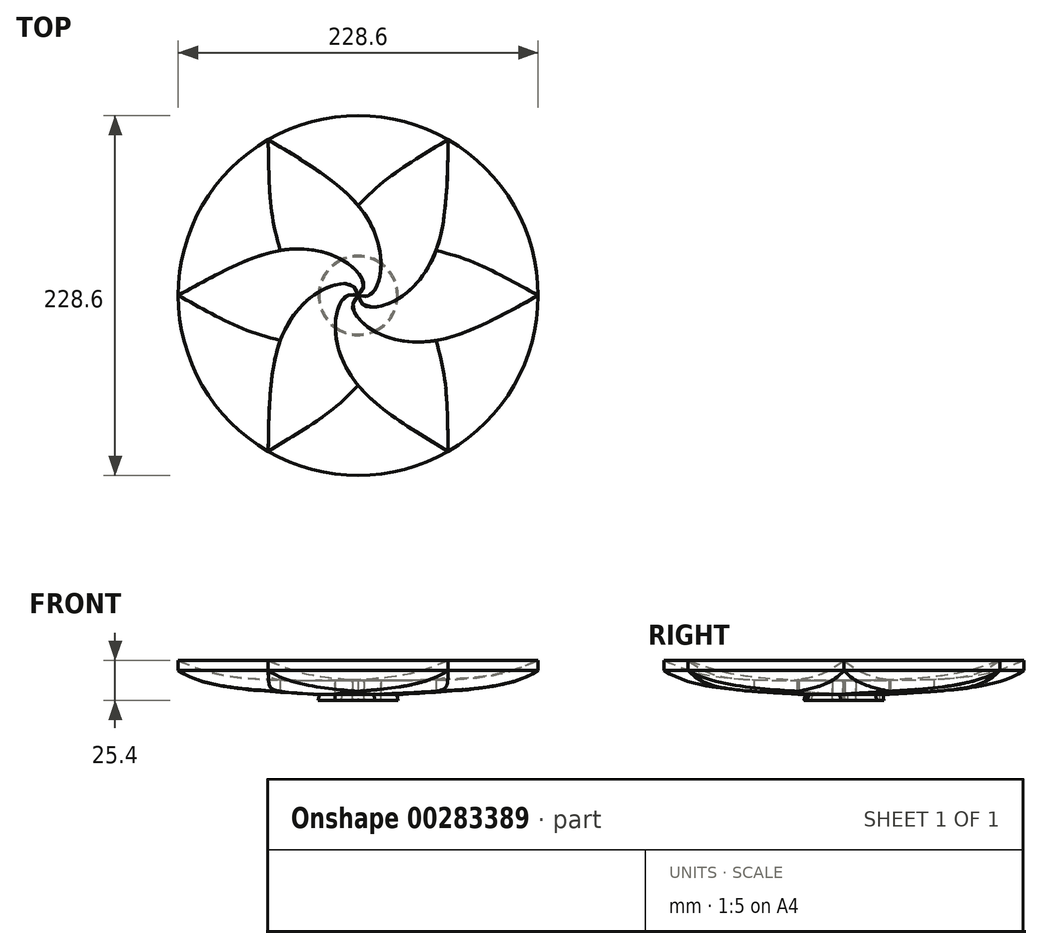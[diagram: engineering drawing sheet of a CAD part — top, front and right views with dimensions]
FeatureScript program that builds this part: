
annotation { "Feature Type Name" : "Feature", "Feature Type Description" : "" }
export const myFeature = defineFeature(function(context is Context, id is Id, definition is map)
    precondition{}
    {
        {
            var Q0;
            Q0=qCreatedBy(makeId("Top.planeOp"),FACE);
            var sketch = newSketch(context, id + "F0", { "sketchPlane" : qUnion([Q0])});
            skLineSegment(sketch, "E0", {"start": v(0, 0) * mm, "end": v(114.3, 0) * mm, "construction": true});
            skCircle(sketch, "E1.cCircle", {"center": v(0, 0) * mm, "radius": 114.3 * mm, "construction": true});
            skLineSegment(sketch, "E1.0", {"start": v(114.3, 66) * mm, "end": v(114.3, -66) * mm, "construction": true});
            skLineSegment(sketch, "E1.1", {"start": v(114.3, -66) * mm, "end": v(0, -131.98) * mm, "construction": true});
            skLineSegment(sketch, "E1.2", {"start": v(0, -131.98) * mm, "end": v(-114.3, -66) * mm, "construction": true});
            skLineSegment(sketch, "E1.3", {"start": v(-114.3, -66) * mm, "end": v(-114.3, 66) * mm, "construction": true});
            skLineSegment(sketch, "E1.4", {"start": v(-114.3, 66) * mm, "end": v(0, 131.98) * mm, "construction": true});
            skLineSegment(sketch, "E1.5", {"start": v(0, 131.98) * mm, "end": v(114.3, 66) * mm, "construction": true});
            skPoint(sketch, "E1.0.midPoint", {"position": v(114.3, 0) * mm});
            skLineSegment(sketch, "E2", {"start": v(0, 0) * mm, "end": v(114.3, 66) * mm, "construction": true});
            skLineSegment(sketch, "E3", {"start": v(0, 0) * mm, "end": v(0, 131.98) * mm, "construction": true});
            skLineSegment(sketch, "E4", {"start": v(0, 0) * mm, "end": v(57.15, 98.99) * mm, "construction": true});
            skLineSegment(sketch, "E5", {"start": v(0, 0) * mm, "end": v(0, 57.15) * mm, "construction": true});
            skLineSegment(sketch, "E6", {"start": v(0, 0) * mm, "end": v(14.29, 24.75) * mm, "construction": true});
            skLineSegment(sketch, "E7", {"start": v(0, 0) * mm, "end": v(12.37, 7.14) * mm, "construction": true});
            skLineSegment(sketch, "E8", {"start": v(0, 0) * mm, "end": v(7.14, 0) * mm, "construction": true});
            skFitSpline(sketch, "E9", {"points": [v(-57.15, 98.99) * mm, v(0, 57.15) * mm, v(14.29, 24.75) * mm, v(12.37, 7.14) * mm, v(7.14, 0) * mm, v(0, 0) * mm], "startDerivative": vector(191.8, -114.67) * mm, "endDerivative": vector(-69.14, 12.61) * mm});
            skLineSegment(sketch, "E10", {"start": v(0, 0) * mm, "end": v(114.3, -66) * mm, "construction": true});
            skLineSegment(sketch, "E11", {"start": v(0, 0) * mm, "end": v(57.15, -98.99) * mm, "construction": true});
            skLineSegment(sketch, "E12", {"start": v(0, 0) * mm, "end": v(49.5, 28.58) * mm, "construction": true});
            skLineSegment(sketch, "E13", {"start": v(0, 0) * mm, "end": v(28.58, 0) * mm, "construction": true});
            skLineSegment(sketch, "E14", {"start": v(0, 0) * mm, "end": v(12.37, -7.14) * mm, "construction": true});
            skLineSegment(sketch, "E15", {"start": v(0, 0) * mm, "end": v(3.57, -6.19) * mm, "construction": true});
            skFitSpline(sketch, "E16", {"points": [v(57.15, 98.99) * mm, v(49.5, 28.57) * mm, v(28.58, 0) * mm, v(12.37, -7.14) * mm, v(3.57, -6.19) * mm, v(0, 0) * mm], "startDerivative": vector(-3.41, -223.44) * mm, "endDerivative": vector(-23.64, 66.18) * mm});
            skLineSegment(sketch, "E17", {"start": v(28.57, 115.48) * mm, "end": v(0, 0) * mm, "construction": true});
            skLineSegment(sketch, "E18", {"start": v(0, 0) * mm, "end": v(18.3, 73.97) * mm, "construction": true});
            skFitSpline(sketch, "E19", {"points": [v(57.15, 98.99) * mm, v(18.3, 73.97) * mm, v(0, 57.15) * mm], "startDerivative": vector(-74.29, -44.4) * mm, "endDerivative": vector(-38.16, -38.99) * mm});
            skSolve(sketch);
        }
        {
            var Q0;
            Q0=makeQuery(id+"F0.imprint","IMPRINT",FACE,{"disambiguationData":[TD([[makeQuery(id+"F0.imprint","IMPRINT",EDGE,{"derivedFrom":sQuery(id+"F0.wireOp",EDGE,"E9")}),1.0]])]});
            extrude(context, id + "F1", {"entities" : qUnion([Q0]), "depth" : 25.4 * mm});
        }
        {
            var Q0;
            Q0=makeQuery(id+"F1.opExtrude","SWEPT_BODY",BODY,{"disambiguationData":[OSD([sQuery(id+"F0.wireOp",EDGE,"E9"),sQuery(id+"F0.wireOp",EDGE,"TZXXsanI-fCTB-etiP-ZLQ6-q0ArW132sDCA"),sQuery(id+"F0.wireOp",EDGE,"e2zwRiE5-dgJw-LFtH-64ea-Jk8bidKStY3W"),sQuery(id+"F0.wireOp",EDGE,"E16")])]});
            var Q1;
            Q1=makeQuery(id+"F1.opExtrude","SWEPT_EDGE",EDGE,{"disambiguationData":[OSD([sQuery(id+"F0.wireOp",EDGE,"E9"),sQuery(id+"F0.wireOp",EDGE,"E16")])]});
            transform(context, id + "F2", {"entities" : qUnion([Q0]), "transformType" : TransformType.ROTATION, "transformAxis" : qUnion([Q1]), "angle" : 60 * degree, "makeCopy" : true});
        }
        {
            var Q0;
            Q0=makeQuery(id+"F2.opPattern","COPY",BODY,{"derivedFrom":makeQuery(id+"F1.opExtrude","SWEPT_BODY",BODY,{"disambiguationData":[OSD([sQuery(id+"F0.wireOp",EDGE,"E9"),sQuery(id+"F0.wireOp",EDGE,"TZXXsanI-fCTB-etiP-ZLQ6-q0ArW132sDCA"),sQuery(id+"F0.wireOp",EDGE,"e2zwRiE5-dgJw-LFtH-64ea-Jk8bidKStY3W"),sQuery(id+"F0.wireOp",EDGE,"E16")])]}),"instanceName":"1"});
            var Q1;
            Q1=makeQuery(id+"F1.opExtrude","SWEPT_EDGE",EDGE,{"disambiguationData":[OSD([sQuery(id+"F0.wireOp",EDGE,"E9"),sQuery(id+"F0.wireOp",EDGE,"E16")])]});
            transform(context, id + "F3", {"entities" : qUnion([Q0]), "transformType" : TransformType.ROTATION, "transformAxis" : qUnion([Q1]), "angle" : 60 * degree, "makeCopy" : true});
        }
        {
            var Q0;
            Q0=makeQuery(id+"F3.opPattern","COPY",BODY,{"derivedFrom":makeQuery(id+"F2.opPattern","COPY",BODY,{"derivedFrom":makeQuery(id+"F1.opExtrude","SWEPT_BODY",BODY,{"disambiguationData":[OSD([sQuery(id+"F0.wireOp",EDGE,"E9"),sQuery(id+"F0.wireOp",EDGE,"TZXXsanI-fCTB-etiP-ZLQ6-q0ArW132sDCA"),sQuery(id+"F0.wireOp",EDGE,"e2zwRiE5-dgJw-LFtH-64ea-Jk8bidKStY3W"),sQuery(id+"F0.wireOp",EDGE,"E16")])]}),"instanceName":"1"}),"instanceName":"1"});
            var Q1;
            Q1=makeQuery(id+"F2.opPattern","COPY",BODY,{"derivedFrom":makeQuery(id+"F1.opExtrude","SWEPT_BODY",BODY,{"disambiguationData":[OSD([sQuery(id+"F0.wireOp",EDGE,"E9"),sQuery(id+"F0.wireOp",EDGE,"TZXXsanI-fCTB-etiP-ZLQ6-q0ArW132sDCA"),sQuery(id+"F0.wireOp",EDGE,"e2zwRiE5-dgJw-LFtH-64ea-Jk8bidKStY3W"),sQuery(id+"F0.wireOp",EDGE,"E16")])]}),"instanceName":"1"});
            var Q2;
            Q2=makeQuery(id+"F1.opExtrude","SWEPT_BODY",BODY,{"disambiguationData":[OSD([sQuery(id+"F0.wireOp",EDGE,"E9"),sQuery(id+"F0.wireOp",EDGE,"TZXXsanI-fCTB-etiP-ZLQ6-q0ArW132sDCA"),sQuery(id+"F0.wireOp",EDGE,"e2zwRiE5-dgJw-LFtH-64ea-Jk8bidKStY3W"),sQuery(id+"F0.wireOp",EDGE,"E16")])]});
            var Q3;
            Q3=makeQuery(id+"F1.opExtrude","SWEPT_EDGE",EDGE,{"disambiguationData":[OSD([sQuery(id+"F0.wireOp",EDGE,"E9"),sQuery(id+"F0.wireOp",EDGE,"E16")])]});
            transform(context, id + "F4", {"entities" : qUnion([Q0, Q1, Q2]), "transformType" : TransformType.ROTATION, "transformAxis" : qUnion([Q3]), "angle" : 180 * degree, "makeCopy" : true});
        }
        {
            var Q0;
            Q0=makeQuery(id+"F4.opPattern","COPY",FACE,{"derivedFrom":makeQuery(id+"F3.opPattern","COPY",FACE,{"derivedFrom":makeQuery(id+"F2.opPattern","COPY",FACE,{"derivedFrom":makeQuery(id+"F1.opExtrude","CAP_FACE",FACE,{"disambiguationData":[OSD([sQuery(id+"F0.wireOp",EDGE,"E9"),sQuery(id+"F0.wireOp",EDGE,"E16"),sQuery(id+"F0.wireOp",EDGE,"E19")])],"isStart":false}),"instanceName":"1"}),"instanceName":"1"}),"instanceName":"1"});
            var sketch = newSketch(context, id + "F5", { "sketchPlane" : qUnion([Q0])});
            skCircle(sketch, "E20", {"center": v(0, 0) * mm, "radius": 114.3 * mm});
            skSolve(sketch);
        }
        {
            var Q0;
            Q0=makeQuery(id+"F5.imprint","IMPRINT",FACE,{"disambiguationData":[TD([[makeQuery(id+"F5.imprint","IMPRINT",EDGE,{"derivedFrom":sQuery(id+"F5.wireOp",EDGE,"E20")}),1.0]])]});
            var Q1;
            Q1=makeQuery(id+"F5.imprint","IMPRINT",FACE,{"disambiguationData":[TD([[makeQuery(id+"F5.imprint","IMPRINT",EDGE,{"derivedFrom":makeQuery(id+"F4.opPattern","COPY",EDGE,{"derivedFrom":makeQuery(id+"F3.opPattern","COPY",EDGE,{"derivedFrom":makeQuery(id+"F2.opPattern","COPY",EDGE,{"derivedFrom":makeQuery(id+"F1.opExtrude","CAP_EDGE",EDGE,{"disambiguationData":[OSD([sQuery(id+"F0.wireOp",EDGE,"E9")])],"isStart":false}),"instanceName":"1"}),"instanceName":"1"}),"instanceName":"1"})}),1.0]])]});
            extrude(context, id + "F6", {"entities" : qUnion([Q0, Q1]), "oppositeDirection" : true, "depth" : 25.4 * mm});
        }
        {
            var Q0;
            Q0=makeQuery(id+"F2.opPattern","COPY",BODY,{"derivedFrom":makeQuery(id+"F1.opExtrude","SWEPT_BODY",BODY,{"disambiguationData":[OSD([sQuery(id+"F0.wireOp",EDGE,"E9"),sQuery(id+"F0.wireOp",EDGE,"E16"),sQuery(id+"F0.wireOp",EDGE,"E19")])]}),"instanceName":"1"});
            var Q1;
            Q1=makeQuery(id+"F4.opPattern","COPY",BODY,{"derivedFrom":makeQuery(id+"F2.opPattern","COPY",BODY,{"derivedFrom":makeQuery(id+"F1.opExtrude","SWEPT_BODY",BODY,{"disambiguationData":[OSD([sQuery(id+"F0.wireOp",EDGE,"E9"),sQuery(id+"F0.wireOp",EDGE,"E16"),sQuery(id+"F0.wireOp",EDGE,"E19")])]}),"instanceName":"1"}),"instanceName":"1"});
            var Q2;
            Q2=makeQuery(id+"F3.opPattern","COPY",BODY,{"derivedFrom":makeQuery(id+"F2.opPattern","COPY",BODY,{"derivedFrom":makeQuery(id+"F1.opExtrude","SWEPT_BODY",BODY,{"disambiguationData":[OSD([sQuery(id+"F0.wireOp",EDGE,"E9"),sQuery(id+"F0.wireOp",EDGE,"E16"),sQuery(id+"F0.wireOp",EDGE,"E19")])]}),"instanceName":"1"}),"instanceName":"1"});
            var Q3;
            Q3=makeQuery(id+"F4.opPattern","COPY",BODY,{"derivedFrom":makeQuery(id+"F1.opExtrude","SWEPT_BODY",BODY,{"disambiguationData":[OSD([sQuery(id+"F0.wireOp",EDGE,"E9"),sQuery(id+"F0.wireOp",EDGE,"E16"),sQuery(id+"F0.wireOp",EDGE,"E19")])]}),"instanceName":"1"});
            var Q4;
            Q4=makeQuery(id+"F4.opPattern","COPY",BODY,{"derivedFrom":makeQuery(id+"F3.opPattern","COPY",BODY,{"derivedFrom":makeQuery(id+"F2.opPattern","COPY",BODY,{"derivedFrom":makeQuery(id+"F1.opExtrude","SWEPT_BODY",BODY,{"disambiguationData":[OSD([sQuery(id+"F0.wireOp",EDGE,"E9"),sQuery(id+"F0.wireOp",EDGE,"E16"),sQuery(id+"F0.wireOp",EDGE,"E19")])]}),"instanceName":"1"}),"instanceName":"1"}),"instanceName":"1"});
            var Q5;
            Q5=makeQuery(id+"F1.opExtrude","SWEPT_BODY",BODY,{"disambiguationData":[OSD([sQuery(id+"F0.wireOp",EDGE,"E9"),sQuery(id+"F0.wireOp",EDGE,"E16"),sQuery(id+"F0.wireOp",EDGE,"E19")])]});
            var Q6;
            Q6=makeQuery(id+"F6.opExtrude","SWEPT_BODY",BODY,{"disambiguationData":[OSD([sQuery(id+"F5.wireOp",EDGE,"E20")])]});
            booleanBodies(context, id + "F7", {"operationType" : BooleanOperationType.SUBTRACTION, "tools" : qUnion([Q0, Q1, Q2, Q3, Q4, Q5]), "targets" : qUnion([Q6]), "keepTools" : true});
        }
        {
            var Q0;
            Q0=qCreatedBy(makeId("Front.planeOp"),FACE);
            var sketch = newSketch(context, id + "F8", { "sketchPlane" : qUnion([Q0])});
            skLineSegment(sketch, "E21", {"start": v(0, 0) * mm, "end": v(0, 12.7) * mm});
            skLineSegment(sketch, "E22", {"start": v(0, 12.7) * mm, "end": v(-114.3, 12.7) * mm, "construction": true});
            skLineSegment(sketch, "E23", {"start": v(-114.3, 12.7) * mm, "end": v(-114.3, 25.4) * mm, "construction": true});
            skFitSpline(sketch, "E24", {"points": [v(-114.3, 25.4) * mm, v(-77, 14.6) * mm, v(0, 12.7) * mm], "startDerivative": vector(90.35, -40.4) * mm, "endDerivative": vector(131.25, 0) * mm});
            skLineSegment(sketch, "E25", {"start": v(0, 0) * mm, "end": v(-25.4, 0) * mm});
            skLineSegment(sketch, "E26", {"start": v(-25.4, 0) * mm, "end": v(-24.56, 3.65) * mm});
            skLineSegment(sketch, "E27", {"start": v(-114.3, 25.4) * mm, "end": v(-114.3, 19.05) * mm});
            skFitSpline(sketch, "E28", {"points": [v(-114.3, 19.05) * mm, v(-80.58, 8.1) * mm, v(-24.56, 3.65) * mm], "startDerivative": vector(65.57, -43.03) * mm, "endDerivative": vector(113.17, -7.4) * mm});
            skSolve(sketch);
        }
        {
            var Q0;
            Q0 = qSketchRegion(id + "F8", true);
            var Q1;
            Q1=sQuery(id+"F8.wireOp",EDGE,"E21");
            revolve(context, id + "F9", {"entities" : qUnion([Q0]), "axis" : qUnion([Q1]), "revolveType" : RevolveType.FULL});
        }
        {
            var Q0;
            Q0=qCreatedBy(makeId("Top.planeOp"),FACE);
            var sketch = newSketch(context, id + "F10", { "sketchPlane" : qUnion([Q0])});
            skCircle(sketch, "E29", {"center": v(0, 0) * mm, "radius": 127 * mm});
            skSolve(sketch);
        }
        {
            var Q0;
            Q0=makeQuery(id+"F10.imprint","IMPRINT",FACE,{"disambiguationData":[TD([[makeQuery(id+"F10.imprint","IMPRINT",EDGE,{"derivedFrom":sQuery(id+"F10.wireOp",EDGE,"E29")}),1.0]])]});
            extrude(context, id + "F11", {"entities" : qUnion([Q0]), "depth" : 25.4 * mm});
        }
        {
            var Q0;
            Q0=makeQuery(id+"F9.opRevolve","SWEPT_BODY",BODY,{"disambiguationData":[OSD([sQuery(id+"F8.wireOp",EDGE,"E21"),sQuery(id+"F8.wireOp",EDGE,"E24"),sQuery(id+"F8.wireOp",EDGE,"E25"),sQuery(id+"F8.wireOp",EDGE,"E26"),sQuery(id+"F8.wireOp",EDGE,"E27"),sQuery(id+"F8.wireOp",EDGE,"E28")])]});
            var Q1;
            Q1=makeQuery(id+"F11.opExtrude","SWEPT_BODY",BODY,{"disambiguationData":[OSD([sQuery(id+"F10.wireOp",EDGE,"E29")])]});
            booleanBodies(context, id + "F12", {"operationType" : BooleanOperationType.SUBTRACTION, "tools" : qUnion([Q0]), "targets" : qUnion([Q1])});
        }
        {
            var Q0;
            Q0=makeQuery(id+"F12.opBoolean","SPLIT",BODY,{"disambiguationData":[OD(1.0)],"derivedFrom":makeQuery(id+"F11.opExtrude","SWEPT_BODY",BODY,{"disambiguationData":[OSD([sQuery(id+"F10.wireOp",EDGE,"E29")])]})});
            var Q1;
            Q1=makeQuery(id+"F12.opBoolean","SPLIT",BODY,{"disambiguationData":[OD(0.0)],"derivedFrom":makeQuery(id+"F11.opExtrude","SWEPT_BODY",BODY,{"disambiguationData":[OSD([sQuery(id+"F10.wireOp",EDGE,"E29")])]})});
            var Q2;
            Q2=makeQuery(id+"F7.opBoolean","SPLIT",BODY,{"disambiguationData":[OD(5.0)],"derivedFrom":makeQuery(id+"F6.opExtrude","SWEPT_BODY",BODY,{"disambiguationData":[OSD([sQuery(id+"F5.wireOp",EDGE,"E20")])]})});
            var Q3;
            Q3=makeQuery(id+"F1.opExtrude","SWEPT_BODY",BODY,{"disambiguationData":[OSD([sQuery(id+"F0.wireOp",EDGE,"E9"),sQuery(id+"F0.wireOp",EDGE,"E16"),sQuery(id+"F0.wireOp",EDGE,"E19")])]});
            var Q4;
            Q4=makeQuery(id+"F2.opPattern","COPY",BODY,{"derivedFrom":makeQuery(id+"F1.opExtrude","SWEPT_BODY",BODY,{"disambiguationData":[OSD([sQuery(id+"F0.wireOp",EDGE,"E9"),sQuery(id+"F0.wireOp",EDGE,"E16"),sQuery(id+"F0.wireOp",EDGE,"E19")])]}),"instanceName":"1"});
            var Q5;
            Q5=makeQuery(id+"F3.opPattern","COPY",BODY,{"derivedFrom":makeQuery(id+"F2.opPattern","COPY",BODY,{"derivedFrom":makeQuery(id+"F1.opExtrude","SWEPT_BODY",BODY,{"disambiguationData":[OSD([sQuery(id+"F0.wireOp",EDGE,"E9"),sQuery(id+"F0.wireOp",EDGE,"E16"),sQuery(id+"F0.wireOp",EDGE,"E19")])]}),"instanceName":"1"}),"instanceName":"1"});
            var Q6;
            Q6=makeQuery(id+"F4.opPattern","COPY",BODY,{"derivedFrom":makeQuery(id+"F1.opExtrude","SWEPT_BODY",BODY,{"disambiguationData":[OSD([sQuery(id+"F0.wireOp",EDGE,"E9"),sQuery(id+"F0.wireOp",EDGE,"E16"),sQuery(id+"F0.wireOp",EDGE,"E19")])]}),"instanceName":"1"});
            var Q7;
            Q7=makeQuery(id+"F4.opPattern","COPY",BODY,{"derivedFrom":makeQuery(id+"F2.opPattern","COPY",BODY,{"derivedFrom":makeQuery(id+"F1.opExtrude","SWEPT_BODY",BODY,{"disambiguationData":[OSD([sQuery(id+"F0.wireOp",EDGE,"E9"),sQuery(id+"F0.wireOp",EDGE,"E16"),sQuery(id+"F0.wireOp",EDGE,"E19")])]}),"instanceName":"1"}),"instanceName":"1"});
            var Q8;
            Q8=makeQuery(id+"F4.opPattern","COPY",BODY,{"derivedFrom":makeQuery(id+"F3.opPattern","COPY",BODY,{"derivedFrom":makeQuery(id+"F2.opPattern","COPY",BODY,{"derivedFrom":makeQuery(id+"F1.opExtrude","SWEPT_BODY",BODY,{"disambiguationData":[OSD([sQuery(id+"F0.wireOp",EDGE,"E9"),sQuery(id+"F0.wireOp",EDGE,"E16"),sQuery(id+"F0.wireOp",EDGE,"E19")])]}),"instanceName":"1"}),"instanceName":"1"}),"instanceName":"1"});
            var Q9;
            Q9=makeQuery(id+"F7.opBoolean","SPLIT",BODY,{"disambiguationData":[OD(0.0)],"derivedFrom":makeQuery(id+"F6.opExtrude","SWEPT_BODY",BODY,{"disambiguationData":[OSD([sQuery(id+"F5.wireOp",EDGE,"E20")])]})});
            var Q10;
            Q10=makeQuery(id+"F7.opBoolean","SPLIT",BODY,{"disambiguationData":[OD(1.0)],"derivedFrom":makeQuery(id+"F6.opExtrude","SWEPT_BODY",BODY,{"disambiguationData":[OSD([sQuery(id+"F5.wireOp",EDGE,"E20")])]})});
            var Q11;
            Q11=makeQuery(id+"F7.opBoolean","SPLIT",BODY,{"disambiguationData":[OD(2.0)],"derivedFrom":makeQuery(id+"F6.opExtrude","SWEPT_BODY",BODY,{"disambiguationData":[OSD([sQuery(id+"F5.wireOp",EDGE,"E20")])]})});
            var Q12;
            Q12=makeQuery(id+"F7.opBoolean","SPLIT",BODY,{"disambiguationData":[OD(3.0)],"derivedFrom":makeQuery(id+"F6.opExtrude","SWEPT_BODY",BODY,{"disambiguationData":[OSD([sQuery(id+"F5.wireOp",EDGE,"E20")])]})});
            var Q13;
            Q13=makeQuery(id+"F7.opBoolean","SPLIT",BODY,{"disambiguationData":[OD(4.0)],"derivedFrom":makeQuery(id+"F6.opExtrude","SWEPT_BODY",BODY,{"disambiguationData":[OSD([sQuery(id+"F5.wireOp",EDGE,"E20")])]})});
            booleanBodies(context, id + "F13", {"operationType" : BooleanOperationType.SUBTRACTION, "tools" : qUnion([Q0, Q1]), "targets" : qUnion([Q2, Q3, Q4, Q5, Q6, Q7, Q8, Q9, Q10, Q11, Q12, Q13])});
        }
    });
